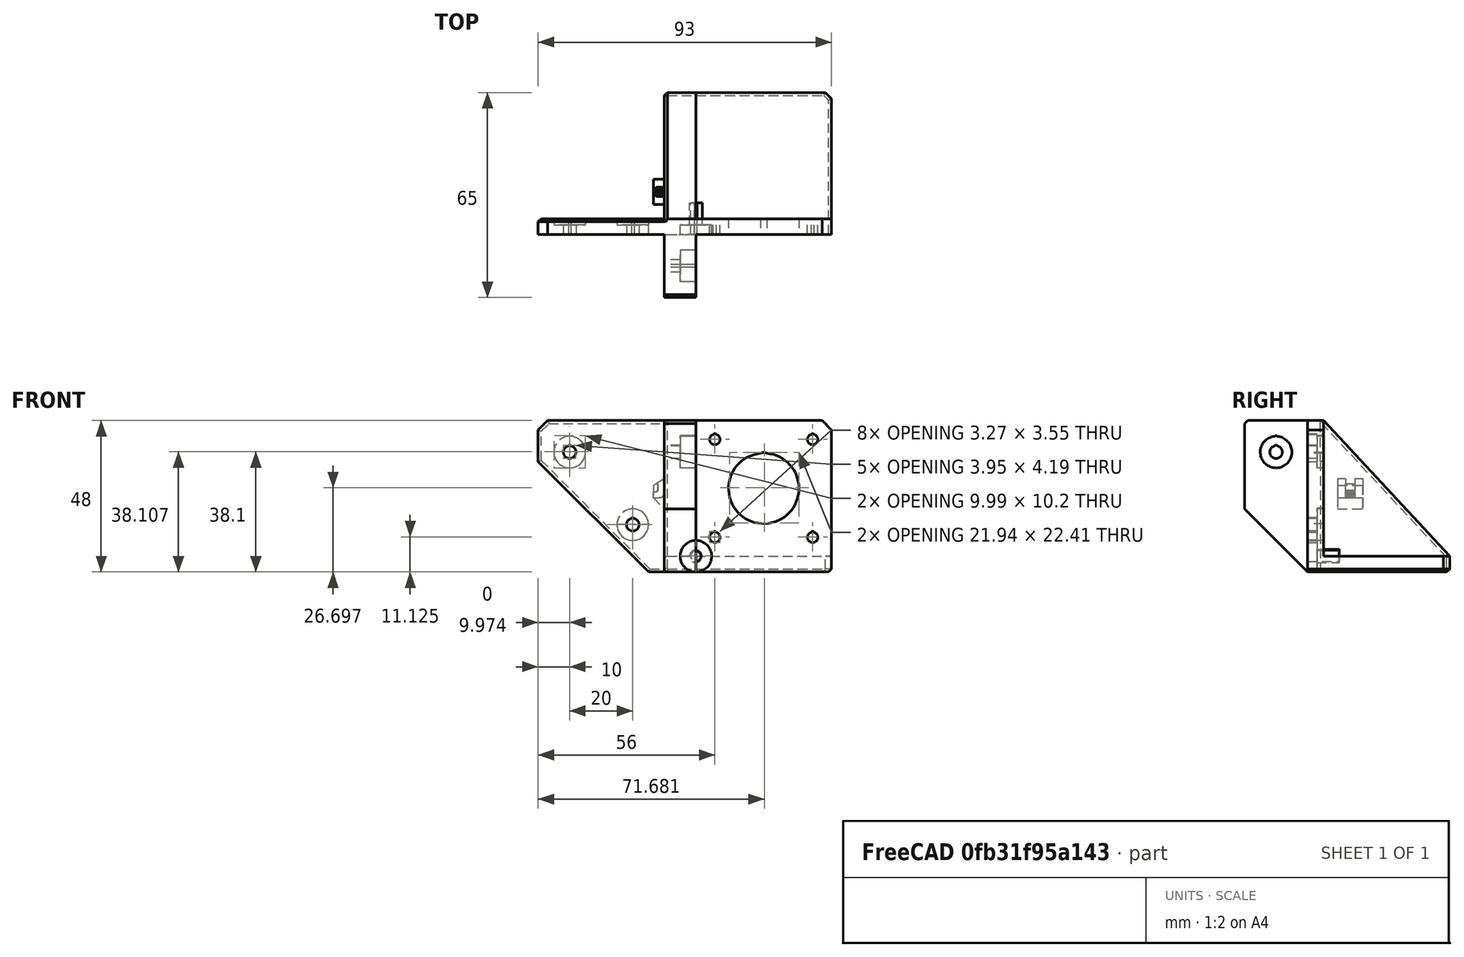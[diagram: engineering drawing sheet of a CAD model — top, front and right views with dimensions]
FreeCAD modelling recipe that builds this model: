
FCSTD DOCUMENT  (FreeCAD 0.18R16146 (Git))
Label: mounter
License: All rights reserved
LicenseURL: http://en.wikipedia.org/wiki/All_rights_reserved
objects: Part::Chamfer×11, Part::Feature×10, Part::Cylinder×8, Part::MultiFuse×7, Part::Box×5, Part::Cut×4
note: 45 computed .brp shape members not serialized (recipe doc carries the construction recipe); baked Part::Feature solids carry a one-line shape summary decoded from their .brp

FEATURE [Part::Box] Box  label="Cube"
  AttacherType = Attacher::AttachEngine3D
  Height = 43
  Length = 43
  Width = 5
FEATURE [Part::Box] Box001  label="Cube001"
  AttacherType = Attacher::AttachEngine3D
  Height = 48
  Length = 45
  Placement = pos=(-45,0,-5) rot=(0,0,1;0rad)
  Width = 5
FEATURE [Part::Box] Box002  label="Cube002"
  AttacherType = Attacher::AttachEngine3D
  Height = 5
  Length = 43
  Placement = pos=(0,0,-5) rot=(0,0,1;0rad)
  Width = 45
FEATURE [Part::Box] Box004  label="Cube004"
  AttacherType = Attacher::AttachEngine3D
  Height = 48
  Length = 10
  Placement = pos=(-10,0,-5) rot=(0,0,1;0rad)
  Width = 45
FEATURE [Part::Box] Box005  label="Cube005"
  AttacherType = Attacher::AttachEngine3D
  Height = 48
  Length = 10
  Placement = pos=(-10,-20,-5) rot=(0,0,1;0rad)
  Width = 21
FEATURE [Part::Cylinder] Cylinder
  Angle = 360
  AttacherType = Attacher::AttachEngine3D
  Height = 10
  Placement = pos=(0,0,1.7) rot=(-1,0,0;1.5708rad)
  Radius = 0.5
FEATURE [Part::Cylinder] Cylinder001
  Angle = 360
  AttacherType = Attacher::AttachEngine3D
  Height = 3
  Placement = pos=(0,-1e-15,4.7) rot=(-1,0,0;1.5708rad)
  Radius = 0.5
FEATURE [Part::Cylinder] Cylinder002
  Angle = 360
  AttacherType = Attacher::AttachEngine3D
  Height = 3
  Placement = pos=(0,0,0) rot=(-1,0,0;1.5708rad)
  Radius = 5
FEATURE [Part::Cylinder] Cylinder003
  Angle = 360
  AttacherType = Attacher::AttachEngine3D
  Height = 10
  Placement = pos=(0,0,0) rot=(-1,0,0;1.5708rad)
  Radius = 2
FEATURE [Part::MultiFuse] Fusion001  label="m4"
  Shapes = -> [Cylinder,Cylinder002,Cylinder003,Cylinder001]
FEATURE [Part::Feature] Fusion001001  label="m005"
  Placement = pos=(-15,5,10) rot=(0,0,1;3.14159rad)
  shape: bbox 10 x 10 x 10.2 mm, 7 faces (baked)
FEATURE [Part::Feature] Fusion001002  label="m006"
  Placement = pos=(-35,5,33) rot=(0,0,1;3.14159rad)
  shape: bbox 10 x 10 x 10.2 mm, 7 faces (baked)
FEATURE [Part::Feature] Fusion001003  label="m007"
  Placement = pos=(-2.2e-15,-10,33) rot=(0,0,1;1.5708rad)
  shape: bbox 10 x 10 x 10.2 mm, 7 faces (baked)
FEATURE [Part::Chamfer] Chamfer
  Base = -> Box001
  Edges = 1 edges r=35: [Edge4]
FEATURE [Part::MultiFuse] Fusion
  Placement = pos=(0,1,0) rot=(0,0,1;0rad)
  Shapes = -> [Fusion001002,Fusion001001]
FEATURE [Part::Cut] Cut
  Base = -> Chamfer
  Tool = -> Fusion
FEATURE [Part::Chamfer] Chamfer003
  Base = -> Cut
  Edges = 1 edges r=3: [Edge3]
FEATURE [Part::Chamfer] Chamfer005
  Base = -> Box
  Edges = 1 edges r=3: [Edge6]
FEATURE [Part::Chamfer] Chamfer006
  Base = -> Box002
  Edges = 1 edges r=2: [Edge7]
FEATURE [Part::Cylinder] Cylinder004
  Angle = 360
  AttacherType = Attacher::AttachEngine3D
  Height = 10
  Placement = pos=(21.5,5,21.5) rot=(1,0,0;1.5708rad)
  Radius = 11.15
FEATURE [Part::Cylinder] Cylinder005
  Angle = 360
  AttacherType = Attacher::AttachEngine3D
  Height = 10
  Placement = pos=(0,0,0) rot=(-1,0,0;1.5708rad)
  Radius = 1.65
FEATURE [Part::Cylinder] Cylinder006
  Angle = 360
  AttacherType = Attacher::AttachEngine3D
  Height = 10
  Placement = pos=(0,0,1.4) rot=(-1,0,0;1.5708rad)
  Radius = 0.5
FEATURE [Part::MultiFuse] Fusion001005  label="m3"
  Shapes = -> [Cylinder006,Cylinder005]
FEATURE [Part::Feature] Fusion001005001  label="m008"
  Placement = pos=(37,0,37) rot=(0,0,1;0rad)
  shape: bbox 3.3 x 10 x 3.55 mm, 4 faces (baked)
FEATURE [Part::Feature] Fusion001005002  label="m009"
  Placement = pos=(6,0,37) rot=(0,0,1;0rad)
  shape: bbox 3.3 x 10 x 3.55 mm, 4 faces (baked)
FEATURE [Part::Feature] Fusion001005003  label="m010"
  Placement = pos=(6,0,6) rot=(0,0,1;0rad)
  shape: bbox 3.3 x 10 x 3.55 mm, 4 faces (baked)
FEATURE [Part::Feature] Fusion001005004  label="m011"
  Placement = pos=(37,0,6) rot=(0,0,1;0rad)
  shape: bbox 3.3 x 10 x 3.55 mm, 4 faces (baked)
FEATURE [Part::MultiFuse] Fusion001005005
  Shapes = -> [Fusion001005004,Fusion001005002,Fusion001005001,Fusion001005003]
FEATURE [Part::Cut] Cut002
  Base = -> Chamfer005
  Tool = -> Fusion001005005
FEATURE [Part::Cylinder] Cylinder007
  Angle = 360
  AttacherType = Attacher::AttachEngine3D
  Height = 10
  Placement = pos=(21.5,5,30.9) rot=(1,0,0;1.5708rad)
  Radius = 2
FEATURE [Part::MultiFuse] Fusion001005006
  Shapes = -> [Cylinder004,Cylinder007]
FEATURE [Part::Cut] Cut003
  Base = -> Cut002
  Tool = -> Fusion001005006
FEATURE [Part::Chamfer] Chamfer008
  Base = -> Chamfer003
  Edges = 5 edges r=1: [Edge4,Edge15,Edge17,Edge18,Edge19]
  Placement = pos=(-5,0,0) rot=(0,0,1;0rad)
FEATURE [Part::Chamfer] Chamfer009
  Base = -> Chamfer006
  Edges = 3 edges r=1: [Edge4,Edge9,Edge13]
FEATURE [Part::Feature] Part__Feature  label="Common002"
  Placement = pos=(-72.74,32,-5.5) rot=(0,0,-1;1.5708rad)
  shape: bbox 3.5 x 8 x 9.5 mm, 30 faces (baked)
FEATURE [Part::Chamfer] Chamfer010
  Base = -> Box004
  Edges = 1 edges: [Edge12 r1=43 r2=40]
FEATURE [Part::Chamfer] Chamfer011
  Base = -> Chamfer010
  Edges = 1 edges r=1: [Edge14]
FEATURE [Part::Feature] Fusion001005007  label="m012"
  Placement = pos=(-2,-10,33) rot=(0,0,1;1.5708rad)
  shape: bbox 10 x 10 x 10.2 mm, 7 faces (baked)
FEATURE [Part::MultiFuse] Fusion001005008
  Shapes = -> [Fusion001005007,Fusion001003]
FEATURE [Part::Cut] Cut004
  Base = -> Box005
  Tool = -> Fusion001005008
FEATURE [Part::Chamfer] Chamfer012
  Base = -> Cut004
  Edges = 1 edges r=1: [Edge10]
FEATURE [Part::Chamfer] Chamfer013
  Base = -> Chamfer012
  Edges = 1 edges r=20: [Edge11]
FEATURE [Part::Chamfer] Chamfer014
  Base = -> Chamfer011
  Edges = 4 edges r=1: [Edge1,Edge2,Edge3,Edge4]
FEATURE [Part::MultiFuse] Fusion001005009
  Shapes = -> [Chamfer014,Chamfer009,Part__Feature,Chamfer008,Chamfer013,Cut003]
FEATURE [Part::Feature] Fusion001005009001  label="Fusion001005010"
  shape: bbox 93 x 65 x 48 mm, 88 faces (baked)
